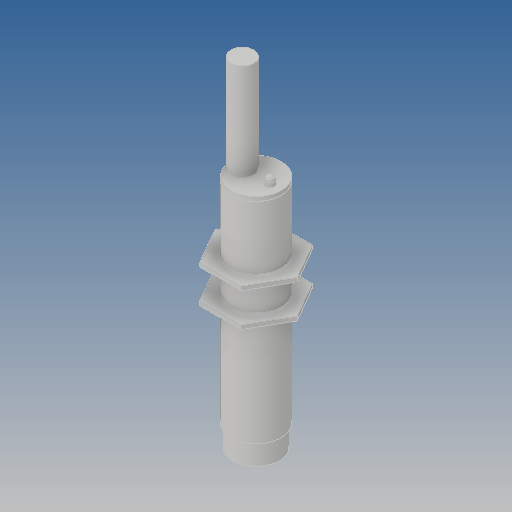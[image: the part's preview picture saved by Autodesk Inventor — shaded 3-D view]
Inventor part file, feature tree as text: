
AUTODESK INVENTOR PART (.ipt)
format: ipt  version: 2018 (Build 220112000, 112)  size: 151,040 bytes
history: native  units: mm
features: other x4, fillet x1
ambient origin geometry x8: Origin, YZ Plane, XZ Plane, XY Plane, X Axis, Y Axis, Z Axis, Center Point
bodies: Solid1 (feature_tree), Solid2 (feature_tree), Solid3 (feature_tree), Solid4 (feature_tree), Solid5 (feature_tree)
feature tree (5):
  other  "Boss-Extrude2"
  other  "Boss-Extrude3"
  other  "Boss-Extrude4"
  fillet  "Fillet1"  [1 undecoded]
  other  "Boss-Extrude7"
note: 1 required parameter value undecoded (feature->parameter linkage not recoverable at this tier; creation-order binding heuristic only, values carry confidence <= 0.55)
